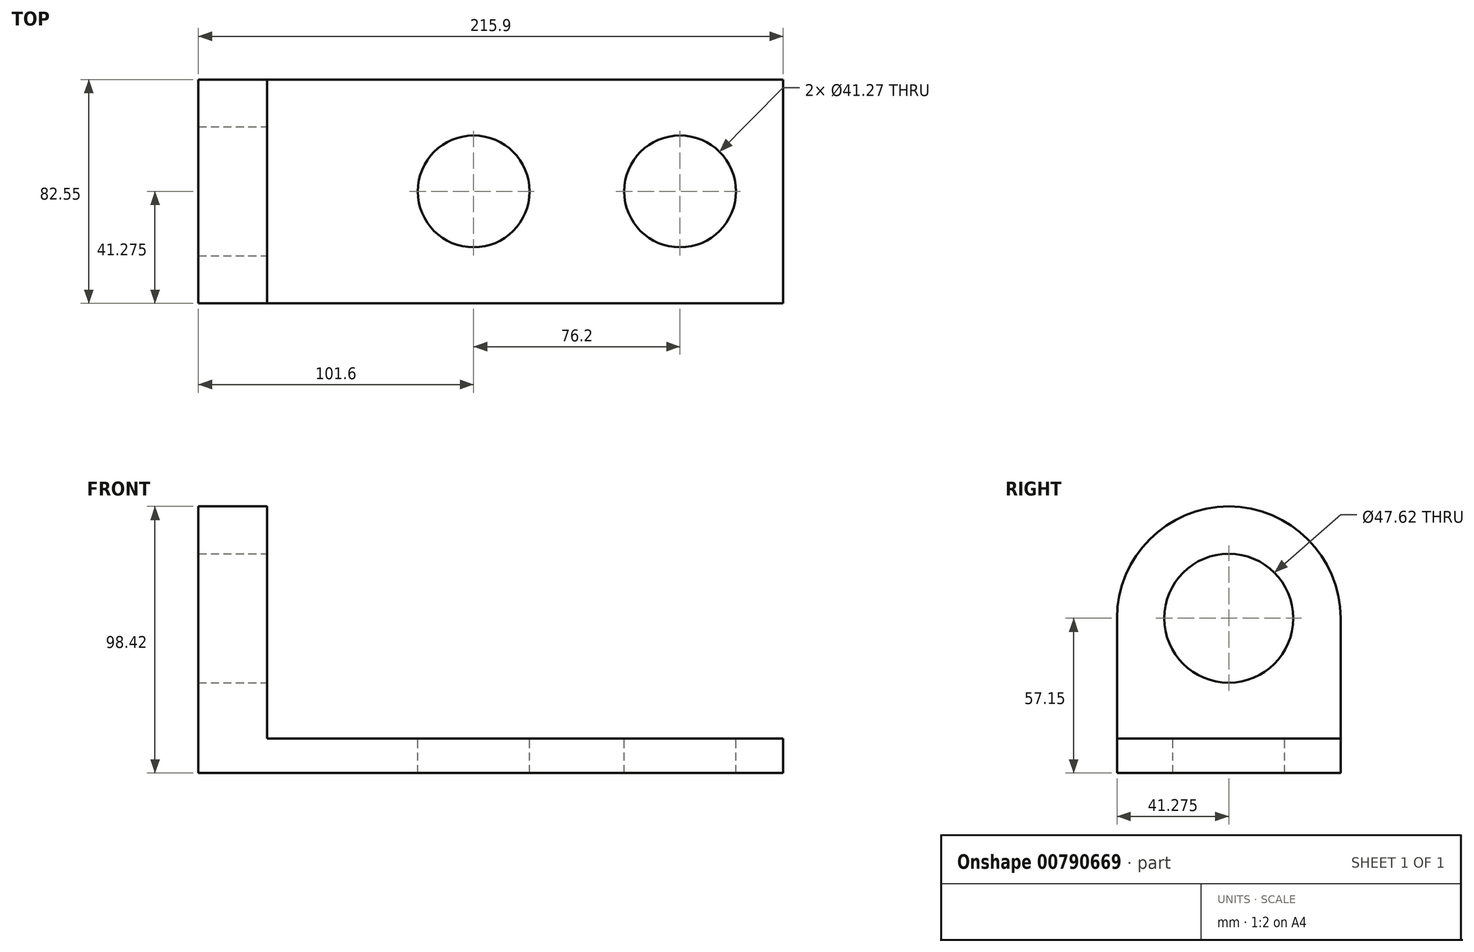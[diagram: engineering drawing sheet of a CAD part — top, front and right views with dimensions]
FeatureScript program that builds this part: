
annotation { "Feature Type Name" : "Feature", "Feature Type Description" : "" }
export const myFeature = defineFeature(function(context is Context, id is Id, definition is map)
    precondition{}
    {
        {
            var Q0;
            Q0=qCreatedBy(makeId("Front.planeOp"),FACE);
            var sketch = newSketch(context, id + "F0", { "sketchPlane" : qUnion([Q0])});
            skLineSegment(sketch, "E0", {"start": v(0, 0) * mm, "end": v(190.5, 0) * mm});
            skLineSegment(sketch, "E1", {"start": v(190.5, 0) * mm, "end": v(190.5, 12.7) * mm});
            skLineSegment(sketch, "E2", {"start": v(0, 0) * mm, "end": v(0, 12.7) * mm});
            skLineSegment(sketch, "E3", {"start": v(190.5, 12.7) * mm, "end": v(0, 12.7) * mm});
            skSolve(sketch);
        }
        {
            var Q0;
            Q0=makeQuery(id+"F0.imprint","IMPRINT",FACE,{"disambiguationData":[TD([[makeQuery(id+"F0.imprint","IMPRINT",EDGE,{"derivedFrom":sQuery(id+"F0.wireOp",EDGE,"E0")}),1.0]])]});
            extrude(context, id + "F1", {"entities" : qUnion([Q0]), "depth" : 82.55 * mm, "offsetDistance" : 25.4 * mm});
        }
        {
            var Q0;
            Q0=makeQuery(id+"F1.opExtrude","CAP_FACE",FACE,{"disambiguationData":[OSD([sQuery(id+"F0.wireOp",EDGE,"E0"),sQuery(id+"F0.wireOp",EDGE,"E1"),sQuery(id+"F0.wireOp",EDGE,"E2"),sQuery(id+"F0.wireOp",EDGE,"E3")])],"isStart":false});
            var sketch = newSketch(context, id + "F2", { "sketchPlane" : qUnion([Q0])});
            skLineSegment(sketch, "E4", {"start": v(0, 0) * mm, "end": v(-25.4, 0) * mm});
            skLineSegment(sketch, "E5", {"start": v(-25.4, 0) * mm, "end": v(-25.4, 57.15) * mm});
            skLineSegment(sketch, "E6", {"start": v(0, 0) * mm, "end": v(0, 57.15) * mm});
            skLineSegment(sketch, "E7", {"start": v(0, 57.15) * mm, "end": v(-25.4, 57.15) * mm});
            skLineSegment(sketch, "E8", {"start": v(-25.4, 57.15) * mm, "end": v(-25.4, 178.82) * mm});
            skLineSegment(sketch, "E9", {"start": v(-25.4, 178.82) * mm, "end": v(0, 178.82) * mm});
            skLineSegment(sketch, "E10", {"start": v(0, 178.82) * mm, "end": v(0, 57.15) * mm});
            skSolve(sketch);
        }
        {
            var Q0;
            {var subQ1=sQuery(id+"F2.wireOp",EDGE,"E4");Q0=makeQuery(id+"F2.imprint","IMPRINT",FACE,{"disambiguationData":[TD([[makeQuery(id+"F2.imprint","IMPRINT",EDGE,{"derivedFrom":subQ1}),-1.0]])]});}
            extrude(context, id + "F3", {"entities" : qUnion([Q0]), "operationType" : NewBodyOperationType.ADD, "depth" : 0 * mm, "offsetDistance" : 25.4 * mm, "hasSecondDirection" : true, "secondDirectionOppositeDirection" : true, "secondDirectionDepth" : 82.55 * mm});
        }
        {
            var Q0;
            Q0=makeQuery(id+"F3.opExtrude","SWEPT_FACE",FACE,{"disambiguationData":[OSD([sQuery(id+"F2.wireOp",EDGE,"E7")])]});
            extrude(context, id + "F4", {"entities" : qUnion([Q0]), "operationType" : NewBodyOperationType.ADD, "depth" : 127 * mm, "offsetDistance" : 25.4 * mm});
        }
        {
            var Q0;
            {var subQ0=sQuery(id+"F2.wireOp",EDGE,"E5");Q0=makeQuery(id+"F4.boolean.opBoolean","MERGE",FACE,{"derivedFrom":[makeQuery(id+"F3.opExtrude","SWEPT_FACE",FACE,{"disambiguationData":[OSD([subQ0])]}),makeQuery(id+"F4.opExtrude","SWEPT_FACE",FACE,{"disambiguationData":[OSD([subQ0,sQuery(id+"F2.wireOp",EDGE,"E7"),sQuery(id+"F2.wireOp",EDGE,"E8")])]})]});}
            var sketch = newSketch(context, id + "F5", { "sketchPlane" : qUnion([Q0])});
            skLineSegment(sketch, "E11", {"start": v(0, 0) * mm, "end": v(0, 57.15) * mm});
            skLineSegment(sketch, "E12", {"start": v(82.55, 0) * mm, "end": v(82.55, 57.15) * mm});
            skArc(sketch, "E13", {"start": v(82.55, 57.15) * mm, "mid": v(41.28, 98.43) * mm, "end": v(0, 57.15) * mm});
            skSolve(sketch);
        }
        {
            var Q0;
            {var subQ0=sQuery(id+"F5.wireOp",EDGE,"E13");Q0=makeQuery(id+"F5.imprint","IMPRINT",FACE,{"disambiguationData":[TD([[makeQuery(id+"F5.imprint","IMPRINT",EDGE,{"derivedFrom":subQ0}),-1.0]])]});}
            extrude(context, id + "F6", {"entities" : qUnion([Q0]), "operationType" : NewBodyOperationType.REMOVE, "endBound" : BoundingType.THROUGH_ALL, "oppositeDirection" : true, "depth" : 25.4 * mm, "offsetDistance" : 25.4 * mm});
        }
        {
            var Q0;
            {var subQ0=sQuery(id+"F2.wireOp",EDGE,"E6");Q0=makeQuery(id+"F4.boolean.opBoolean","MERGE",FACE,{"derivedFrom":[makeQuery(id+"F3.opExtrude","SWEPT_FACE",FACE,{"disambiguationData":[OSD([subQ0])]}),makeQuery(id+"F4.opExtrude","SWEPT_FACE",FACE,{"disambiguationData":[OSD([subQ0,sQuery(id+"F2.wireOp",EDGE,"E7"),sQuery(id+"F2.wireOp",EDGE,"E10")])]})]});}
            var sketch = newSketch(context, id + "F7", { "sketchPlane" : qUnion([Q0])});
            skCircle(sketch, "E14", {"center": v(-41.28, 57.15) * mm, "radius": 23.81 * mm});
            skSolve(sketch);
        }
        {
            var Q0;
            Q0=makeQuery(id+"F7.imprint","IMPRINT",FACE,{"disambiguationData":[TD([[makeQuery(id+"F7.imprint","IMPRINT",EDGE,{"derivedFrom":sQuery(id+"F7.wireOp",EDGE,"E14")}),1.0]])]});
            extrude(context, id + "F8", {"entities" : qUnion([Q0]), "operationType" : NewBodyOperationType.REMOVE, "endBound" : BoundingType.THROUGH_ALL, "oppositeDirection" : true, "depth" : 25.4 * mm, "offsetDistance" : 25.4 * mm});
        }
        {
            var Q0;
            Q0=makeQuery(id+"F1.opExtrude","SWEPT_FACE",FACE,{"disambiguationData":[OSD([sQuery(id+"F0.wireOp",EDGE,"E3")])]});
            var sketch = newSketch(context, id + "F9", { "sketchPlane" : qUnion([Q0])});
            skLineSegment(sketch, "E15", {"start": v(190.5, 0) * mm, "end": v(152.4, 0) * mm});
            skLineSegment(sketch, "E16", {"start": v(152.4, 0) * mm, "end": v(76.2, 0) * mm});
            skLineSegment(sketch, "E17", {"start": v(76.2, 0) * mm, "end": v(76.2, -82.55) * mm});
            skPoint(sketch, "E17.endSnap0", {"position": v(95.25, -82.55) * mm});
            skLineSegment(sketch, "E18", {"start": v(152.4, 0) * mm, "end": v(152.4, -82.55) * mm});
            skCircle(sketch, "E19", {"center": v(76.2, -41.28) * mm, "radius": 20.64 * mm});
            skCircle(sketch, "E20", {"center": v(152.4, -41.28) * mm, "radius": 20.64 * mm});
            skSolve(sketch);
        }
        {
            var Q0;
            {var subQ0=sQuery(id+"F9.wireOp",EDGE,"E19");var subQ1=sQuery(id+"F9.wireOp",EDGE,"E17");var subQ2=makeQuery(id+"F9.imprint","INTERSECT",VERTEX,{"disambiguationData":[OD(0.0)],"derivedFrom":[subQ1,subQ0]});Q0=makeQuery(id+"F9.imprint","IMPRINT",FACE,{"disambiguationData":[TD([[makeQuery(id+"F9.imprint","IMPRINT",EDGE,{"disambiguationData":[TD([[subQ2,-1.0]])],"derivedFrom":subQ1}),1.0]])]});}
            var Q1;
            {var subQ0=sQuery(id+"F9.wireOp",EDGE,"E19");var subQ1=sQuery(id+"F9.wireOp",EDGE,"E17");var subQ2=makeQuery(id+"F9.imprint","INTERSECT",VERTEX,{"disambiguationData":[OD(0.0)],"derivedFrom":[subQ1,subQ0]});Q1=makeQuery(id+"F9.imprint","IMPRINT",FACE,{"disambiguationData":[TD([[makeQuery(id+"F9.imprint","IMPRINT",EDGE,{"disambiguationData":[TD([[subQ2,-1.0]])],"derivedFrom":subQ1}),-1.0]])]});}
            var Q2;
            {var subQ0=sQuery(id+"F9.wireOp",EDGE,"E20");var subQ1=sQuery(id+"F9.wireOp",EDGE,"E18");var subQ2=makeQuery(id+"F9.imprint","INTERSECT",VERTEX,{"disambiguationData":[OD(0.0)],"derivedFrom":[subQ1,subQ0]});Q2=makeQuery(id+"F9.imprint","IMPRINT",FACE,{"disambiguationData":[TD([[makeQuery(id+"F9.imprint","IMPRINT",EDGE,{"disambiguationData":[TD([[subQ2,-1.0]])],"derivedFrom":subQ1}),1.0]])]});}
            var Q3;
            {var subQ0=sQuery(id+"F9.wireOp",EDGE,"E20");var subQ1=sQuery(id+"F9.wireOp",EDGE,"E18");var subQ2=makeQuery(id+"F9.imprint","INTERSECT",VERTEX,{"disambiguationData":[OD(0.0)],"derivedFrom":[subQ1,subQ0]});Q3=makeQuery(id+"F9.imprint","IMPRINT",FACE,{"disambiguationData":[TD([[makeQuery(id+"F9.imprint","IMPRINT",EDGE,{"disambiguationData":[TD([[subQ2,-1.0]])],"derivedFrom":subQ1}),-1.0]])]});}
            extrude(context, id + "F10", {"entities" : qUnion([Q0, Q1, Q2, Q3]), "operationType" : NewBodyOperationType.REMOVE, "endBound" : BoundingType.THROUGH_ALL, "oppositeDirection" : true, "depth" : 25.4 * mm, "offsetDistance" : 25.4 * mm});
        }
    });
